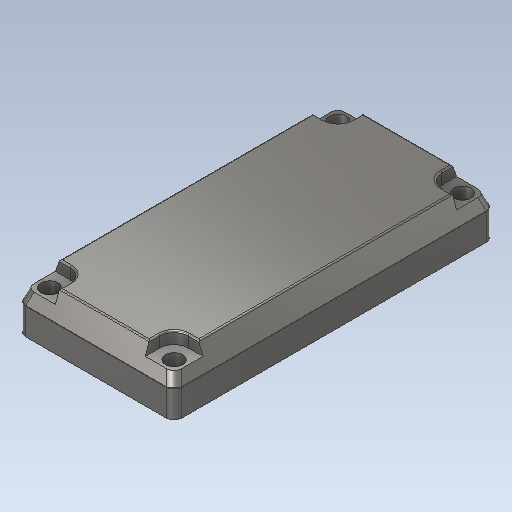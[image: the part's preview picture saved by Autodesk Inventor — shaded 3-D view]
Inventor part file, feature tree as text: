
AUTODESK INVENTOR PART (.ipt)
format: ipt  version: 2020 (Build 240168000, 168)  size: 269,824 bytes
history: native  units: mm
features: other x4, mirror x4, chamfer x4, extrude x3, fillet x2, sketch x2
ambient origin geometry x8: Origin, YZ Plane, XZ Plane, XY Plane, X Axis, Y Axis, Z Axis, Center Point
bodies: Body1 (feature_tree)
feature tree (19):
  other  "Sólido1"
  extrude  "Extrusión1"  Depth=40.6mm
  extrude  "Extrusión2"  Depth=0.2mm
  mirror  "Simetría1"
  mirror  "Simetría2"
  extrude  "Extrusión3"  Depth=0.2mm TaperAngle=0.0deg
  mirror  "Simetría3"
  mirror  "Simetría4"
  chamfer  "Chaflán1"  Distance=2.2mm
  chamfer  "Chaflán2"  Distance=2.2mm
  chamfer  "Chaflán3"  Distance=2.2mm
  chamfer  "Chaflán4"  Distance=1.5mm
  fillet  "Empalme1"  Radius=2.0mm
  fillet  "Empalme2"  Radius=2.0mm
  sketch  "Boceto1"  dims[d0=19.8mm d1=40.6mm]
  other  "Eje de trabajo1"
  other  "Eje de trabajo2"
  other  "Eje de trabajo3"
  sketch  "Boceto4"  dims[d2=6.4mm d3=0.0mm d6=3.6mm d8=1.5mm d9=0.0mm d10=2.2mm d11=2.2mm d12=2.2mm d13=1.5mm d14=0.0mm d15=3.0mm d16=2.0mm d17=3.490659mm d18=3.0mm d19=2.0mm d20=3.490659mm d21=3.0mm d22=2.0mm d23=3.490659mm d24=3.0mm d25=2.0mm d26=3.490659mm d27=1.0mm d28=0.2mm]
